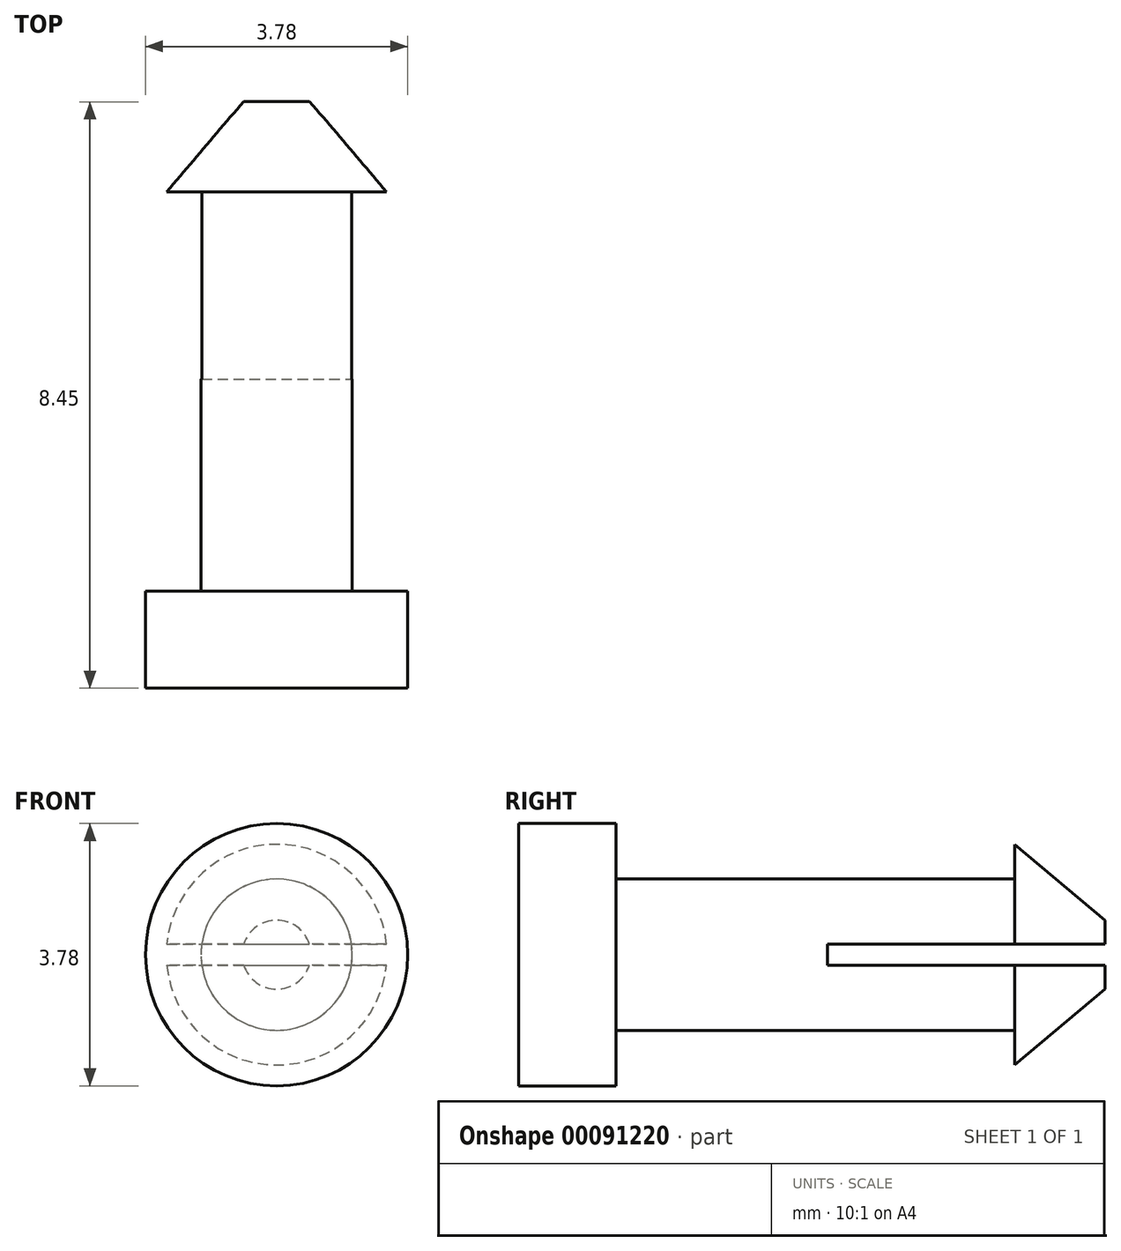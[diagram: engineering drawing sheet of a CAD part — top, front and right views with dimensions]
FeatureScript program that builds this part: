
annotation { "Feature Type Name" : "Feature", "Feature Type Description" : "" }
export const myFeature = defineFeature(function(context is Context, id is Id, definition is map)
    precondition{}
    {
        {
            var Q0;
            Q0=qCreatedBy(makeId("Right.planeOp"),FACE);
            var sketch = newSketch(context, id + "F0", { "sketchPlane" : qUnion([Q0])});
            skLineSegment(sketch, "E0", {"start": v(0, 0) * mm, "end": v(0, 1.89) * mm});
            skLineSegment(sketch, "E1", {"start": v(0, 1.89) * mm, "end": v(1.4, 1.89) * mm});
            skLineSegment(sketch, "E2", {"start": v(1.4, 1.89) * mm, "end": v(1.4, 1.09) * mm});
            skLineSegment(sketch, "E3", {"start": v(1.4, 1.09) * mm, "end": v(7.15, 1.1) * mm});
            skLineSegment(sketch, "E4", {"start": v(7.15, 1.1) * mm, "end": v(7.15, 1.6) * mm});
            skLineSegment(sketch, "E5", {"start": v(7.15, 1.6) * mm, "end": v(8.45, 0.5) * mm});
            skLineSegment(sketch, "E6", {"start": v(4.7, 0) * mm, "end": v(0, 0) * mm});
            skLineSegment(sketch, "E7", {"start": v(8.45, 0.5) * mm, "end": v(8.45, 0) * mm});
            skLineSegment(sketch, "E8", {"start": v(8.45, 0) * mm, "end": v(4.7, 0) * mm});
            skSolve(sketch);
        }
        {
            var Q0;
            Q0=makeQuery(id+"F0.imprint","IMPRINT",FACE,{"disambiguationData":[TD([[makeQuery(id+"F0.imprint","IMPRINT",EDGE,{"derivedFrom":sQuery(id+"F0.wireOp",EDGE,"E0")}),-1.0]])]});
            var Q1;
            Q1=sQuery(id+"F0.wireOp",EDGE,"E8");
            revolve(context, id + "F1", {"entities" : qUnion([Q0]), "axis" : qUnion([Q1]), "revolveType" : RevolveType.FULL});
        }
        {
            var Q0;
            Q0=makeQuery(id+"F1.opRevolve","SWEPT_FACE",FACE,{"disambiguationData":[OSD([sQuery(id+"F0.wireOp",EDGE,"E7")])]});
            var sketch = newSketch(context, id + "F2", { "sketchPlane" : qUnion([Q0])});
            skLineSegment(sketch, "E9.bottom", {"start": v(1.76, 0.15) * mm, "end": v(-1.76, 0.15) * mm});
            skLineSegment(sketch, "E9.top", {"start": v(1.76, -0.15) * mm, "end": v(-1.76, -0.15) * mm});
            skLineSegment(sketch, "E9.left", {"start": v(1.76, 0.15) * mm, "end": v(1.76, -0.15) * mm});
            skLineSegment(sketch, "E9.right", {"start": v(-1.76, 0.15) * mm, "end": v(-1.76, -0.15) * mm});
            skPoint(sketch, "E9.middle", {"position": v(0, 0) * mm});
            skSolve(sketch);
        }
        {
            var Q0;
            Q0 = qSketchRegion(id + "F2", true);
            extrude(context, id + "F3", {"entities" : qUnion([Q0]), "operationType" : NewBodyOperationType.REMOVE, "oppositeDirection" : true, "depth" : 4 * mm});
        }
    });
